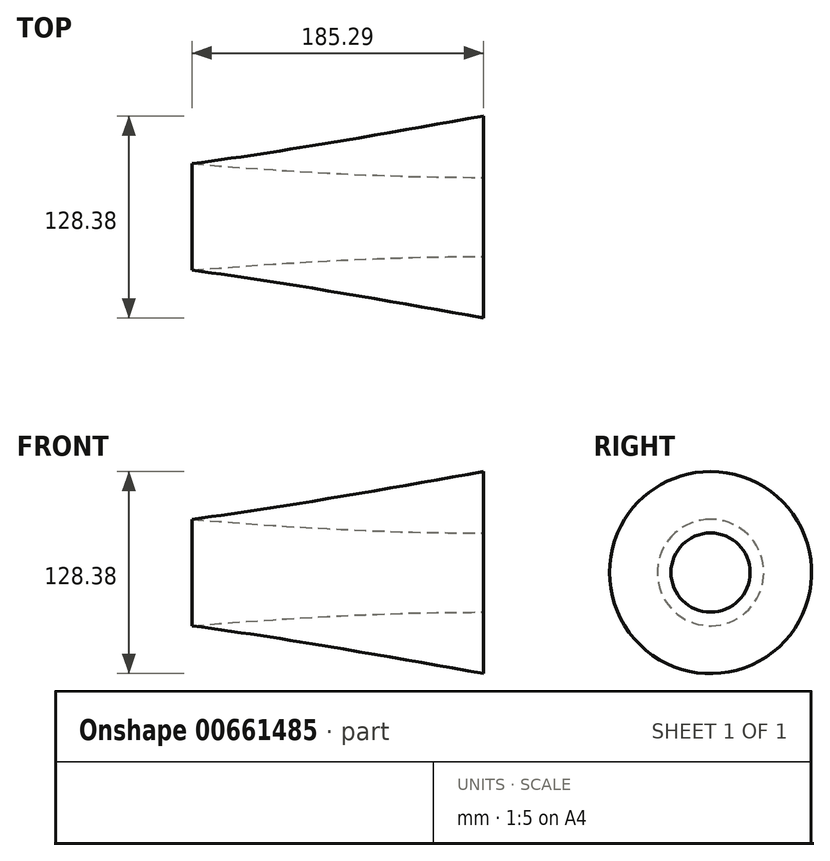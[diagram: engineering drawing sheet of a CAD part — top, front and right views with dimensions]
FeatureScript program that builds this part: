
annotation { "Feature Type Name" : "Feature", "Feature Type Description" : "" }
export const myFeature = defineFeature(function(context is Context, id is Id, definition is map)
    precondition{}
    {
        {
            var Q0;
            Q0=qCreatedBy(makeId("Top.planeOp"),FACE);
            var sketch = newSketch(context, id + "F0", { "sketchPlane" : qUnion([Q0])});
            skLineSegment(sketch, "E0", {"start": v(-185.3, -22.6) * mm, "end": v(0, -59.06) * mm});
            skLineSegment(sketch, "E1", {"start": v(0, -59.06) * mm, "end": v(0, 0) * mm});
            skLineSegment(sketch, "E2", {"start": v(0, 0) * mm, "end": v(-185.3, -22.6) * mm});
            skSolve(sketch);
        }
        {
            var Q0;
            Q0=qCreatedBy(makeId("Front.planeOp"),FACE);
            var sketch = newSketch(context, id + "F1", { "sketchPlane" : qUnion([Q0])});
            skLineSegment(sketch, "E3", {"start": v(-44.53, -25.15) * mm, "end": v(38.6, -25.15) * mm});
            skSolve(sketch);
        }
        {
            var Q0;
            Q0=makeQuery(id+"F0.imprint","IMPRINT",FACE,{"disambiguationData":[TD([[makeQuery(id+"F0.imprint","IMPRINT",EDGE,{"derivedFrom":sQuery(id+"F0.wireOp",EDGE,"E0")}),1.0]])]});
            var Q1;
            Q1=sQuery(id+"F1.wireOp",EDGE,"E3");
            revolve(context, id + "F2", {"entities" : qUnion([Q0]), "axis" : qUnion([Q1]), "revolveType" : RevolveType.FULL});
        }
    });
